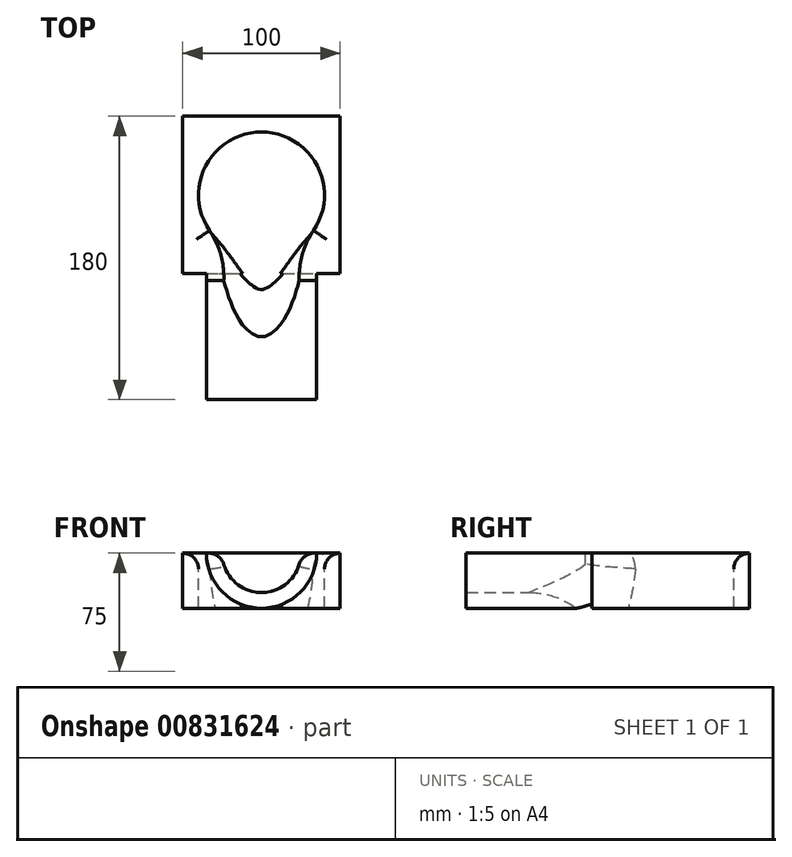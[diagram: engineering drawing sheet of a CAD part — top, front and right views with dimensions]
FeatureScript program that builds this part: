
annotation { "Feature Type Name" : "Feature", "Feature Type Description" : "" }
export const myFeature = defineFeature(function(context is Context, id is Id, definition is map)
    precondition{}
    {
        {
            var Q0;
            Q0=qCreatedBy(makeId("Front.planeOp"),FACE);
            var sketch = newSketch(context, id + "F0", { "sketchPlane" : qUnion([Q0])});
            skCircle(sketch, "E0", {"center": v(0, 0) * mm, "radius": 25 * mm});
            skCircle(sketch, "E1", {"center": v(0, 0) * mm, "radius": 35 * mm});
            skLineSegment(sketch, "E2", {"start": v(35, 0) * mm, "end": v(-35, 0) * mm});
            skSolve(sketch);
        }
        {
            var Q0;
            {var subQ0=sQuery(id+"F0.wireOp",EDGE,"E2");var subQ1=sQuery(id+"F0.wireOp",EDGE,"E0");var subQ2=makeQuery(id+"F0.imprint","INTERSECT",VERTEX,{"disambiguationData":[OD(0.0)],"derivedFrom":[subQ1,subQ0]});Q0=makeQuery(id+"F0.imprint","IMPRINT",FACE,{"disambiguationData":[TD([[makeQuery(id+"F0.imprint","IMPRINT",EDGE,{"disambiguationData":[TD([[subQ2,1.0]])],"derivedFrom":subQ1}),-1.0]])]});}
            extrude(context, id + "F1", {"entities" : qUnion([Q0]), "depth" : 80 * mm, "offsetDistance" : 25 * mm});
        }
        {
            var Q0;
            Q0=makeQuery(id+"F1.opExtrude","CAP_FACE",FACE,{"disambiguationData":[OSD([sQuery(id+"F0.wireOp",EDGE,"E0"),sQuery(id+"F0.wireOp",EDGE,"E1"),sQuery(id+"F0.wireOp",EDGE,"E2")])],"isStart":true});
            var sketch = newSketch(context, id + "F2", { "sketchPlane" : qUnion([Q0])});
            skLineSegment(sketch, "E3", {"start": v(0, -35) * mm, "end": v(0, 0) * mm, "construction": true});
            skLineSegment(sketch, "E4.bottom", {"start": v(50, 0) * mm, "end": v(-50, 0) * mm});
            skLineSegment(sketch, "E4.top", {"start": v(50, -35) * mm, "end": v(-50, -35) * mm});
            skLineSegment(sketch, "E4.left", {"start": v(50, 0) * mm, "end": v(50, -35) * mm});
            skLineSegment(sketch, "E4.right", {"start": v(-50, 0) * mm, "end": v(-50, -35) * mm});
            skPoint(sketch, "E4.middle", {"position": v(0, -17.5) * mm});
            skSolve(sketch);
        }
        {
            var Q0;
            Q0 = qSketchRegion(id + "F2", true);
            extrude(context, id + "F3", {"entities" : qUnion([Q0]), "operationType" : NewBodyOperationType.ADD, "depth" : 100 * mm, "offsetDistance" : 25 * mm});
        }
        {
            var Q0;
            {var subQ0=sQuery(id+"F0.wireOp",EDGE,"E2");var subQ1=sQuery(id+"F0.wireOp",EDGE,"E1");Q0=makeQuery(id+"F3.boolean.opBoolean","MERGE",FACE,{"derivedFrom":[makeQuery(id+"F1.opExtrude","SWEPT_FACE",FACE,{"disambiguationData":[OSD([subQ0]),TDD([makeQuery(id+"F0.imprint","IMPRINT",EDGE,{"disambiguationData":[TD([[makeQuery(id+"F0.imprint","INTERSECT",VERTEX,{"disambiguationData":[OD(0.0)],"derivedFrom":[subQ1,subQ0]}),-1.0]])],"derivedFrom":subQ0})])]}),makeQuery(id+"F1.opExtrude","SWEPT_FACE",FACE,{"disambiguationData":[OSD([subQ0]),TDD([makeQuery(id+"F0.imprint","IMPRINT",EDGE,{"disambiguationData":[TD([[makeQuery(id+"F0.imprint","INTERSECT",VERTEX,{"disambiguationData":[OD(1.0)],"derivedFrom":[subQ1,subQ0]}),1.0]])],"derivedFrom":subQ0})])]}),makeQuery(id+"F3.opExtrude","SWEPT_FACE",FACE,{"disambiguationData":[OSD([sQuery(id+"F2.wireOp",EDGE,"E4.bottom")])]})]});}
            var sketch = newSketch(context, id + "F4", { "sketchPlane" : qUnion([Q0])});
            skCircle(sketch, "E5", {"center": v(0, 50) * mm, "radius": 50 * mm});
            skPoint(sketch, "E5.first.point", {"position": v(0, 0) * mm});
            skPoint(sketch, "E5.second.point", {"position": v(-50, 50) * mm});
            skPoint(sketch, "E5.third.point", {"position": v(50, 50) * mm});
            skSolve(sketch);
        }
        {
            var Q0;
            {var subQ0=sQuery(id+"F4.wireOp",EDGE,"E5");var subQ1=sQuery(id+"F2.wireOp",EDGE,"E4.bottom");var subQ2=makeQuery(id+"F4.imprint","INTERSECT",VERTEX,{"derivedFrom":[makeQuery(id+"F3.opExtrude","CAP_EDGE",EDGE,{"disambiguationData":[OSD([subQ1])],"isStart":false}),subQ0]});Q0=makeQuery(id+"F4.imprint","IMPRINT",FACE,{"disambiguationData":[TD([[makeQuery(id+"F4.imprint","IMPRINT",EDGE,{"disambiguationData":[TD([[subQ2,1.0]])],"derivedFrom":subQ0}),1.0]])]});}
            var sketch = newSketch(context, id + "F5", { "sketchPlane" : qUnion([Q0])});
            skCircle(sketch, "E6", {"center": v(0, 50) * mm, "radius": 40 * mm});
            skSolve(sketch);
        }
        {
            var Q0;
            Q0=makeQuery(id+"F5.imprint","IMPRINT",FACE,{"disambiguationData":[TD([[makeQuery(id+"F5.imprint","IMPRINT",EDGE,{"derivedFrom":sQuery(id+"F5.wireOp",EDGE,"E6")}),1.0]])]});
            extrude(context, id + "F6", {"entities" : qUnion([Q0]), "operationType" : NewBodyOperationType.REMOVE, "endBound" : BoundingType.UP_TO_NEXT, "oppositeDirection" : true, "depth" : 25 * mm, "offsetDistance" : 25 * mm});
        }
        {
            var Q0;
            {var subQ0=sQuery(id+"F0.wireOp",EDGE,"E0");var subQ3=sQuery(id+"F2.wireOp",EDGE,"E4.bottom");Q0=makeQuery(id+"F3.boolean.opBoolean","SPLIT",FACE,{"disambiguationData":[TD([makeQuery(id+"F1.opExtrude","SWEPT_FACE",FACE,{"disambiguationData":[OSD([subQ0])]})])],"derivedFrom":makeQuery(id+"F3.opExtrude","CAP_FACE",FACE,{"disambiguationData":[OSD([subQ3,sQuery(id+"F2.wireOp",EDGE,"E4.top"),sQuery(id+"F2.wireOp",EDGE,"E4.left"),sQuery(id+"F2.wireOp",EDGE,"E4.right")])],"isStart":true})});}
            extrude(context, id + "F7", {"entities" : qUnion([Q0]), "operationType" : NewBodyOperationType.REMOVE, "oppositeDirection" : true, "depth" : 25 * mm, "offsetDistance" : 25 * mm});
        }
        {
            var Q0;
            Q0=makeQuery(id+"F7.boolean.opBoolean","INTERSECT",EDGE,{"derivedFrom":[makeQuery(id+"F6.boolean.opBoolean","COPY",FACE,{"derivedFrom":makeQuery(id+"F6.opExtrude","SWEPT_FACE",FACE,{"disambiguationData":[OSD([sQuery(id+"F5.wireOp",EDGE,"E6")])]})}),makeQuery(id+"F7.opExtrude","SWEPT_FACE",FACE,{"disambiguationData":[OSD([sQuery(id+"F0.wireOp",EDGE,"E0")])]})]});
            fillet(context, id + "F8", {"entities" : qUnion([Q0]), "radius" : 50 * mm, "tangentPropagation" : true, "allowEdgeOverflow" : false});
        }
        {
            var Q0;
            {var subQ0=sQuery(id+"F0.wireOp",EDGE,"E2");var subQ1=sQuery(id+"F0.wireOp",EDGE,"E0");var subQ2=makeQuery(id+"F0.imprint","INTERSECT",VERTEX,{"disambiguationData":[OD(0.0)],"derivedFrom":[subQ1,subQ0]});Q0=makeQuery(id+"F7.boolean.opBoolean","MERGE",EDGE,{"derivedFrom":[makeQuery(id+"F1.opExtrude","SWEPT_EDGE",EDGE,{"disambiguationData":[OSD([subQ1,subQ0]),TDD([subQ2])]}),makeQuery(id+"F7.opExtrude","SWEPT_EDGE",EDGE,{"disambiguationData":[OSD([subQ1,subQ0]),TDD([makeQuery(id+"F1.opExtrude","CAP_VERTEX",VERTEX,{"disambiguationData":[OSD([subQ1,subQ0]),TDD([subQ2])],"isStart":true})])]})]});}
            var Q1;
            Q1=makeQuery(id+"F6.boolean.opBoolean","COPY",EDGE,{"derivedFrom":makeQuery(id+"F6.opExtrude","CAP_EDGE",EDGE,{"disambiguationData":[OSD([sQuery(id+"F5.wireOp",EDGE,"E6")])],"isStart":true})});
            var Q2;
            {var subQ0=sQuery(id+"F0.wireOp",EDGE,"E2");var subQ1=sQuery(id+"F0.wireOp",EDGE,"E1");var subQ2=sQuery(id+"F0.wireOp",EDGE,"E0");Q2=makeQuery(id+"F8.opFillet","BLEND_EDGE",EDGE,{"disambiguationData":[OD(0.0)],"blendedFrom":[makeQuery(id+"F7.boolean.opBoolean","INTERSECT",EDGE,{"derivedFrom":[makeQuery(id+"F6.boolean.opBoolean","COPY",FACE,{"derivedFrom":makeQuery(id+"F6.opExtrude","SWEPT_FACE",FACE,{"disambiguationData":[OSD([sQuery(id+"F5.wireOp",EDGE,"E6")])]})}),makeQuery(id+"F7.opExtrude","SWEPT_FACE",FACE,{"disambiguationData":[OSD([subQ2])]})]}),makeQuery(id+"F3.boolean.opBoolean","MERGE",FACE,{"derivedFrom":[makeQuery(id+"F1.opExtrude","SWEPT_FACE",FACE,{"disambiguationData":[OSD([subQ0]),TDD([makeQuery(id+"F0.imprint","IMPRINT",EDGE,{"disambiguationData":[TD([[makeQuery(id+"F0.imprint","INTERSECT",VERTEX,{"disambiguationData":[OD(0.0)],"derivedFrom":[subQ1,subQ0]}),-1.0]])],"derivedFrom":subQ0})])]}),makeQuery(id+"F1.opExtrude","SWEPT_FACE",FACE,{"disambiguationData":[OSD([subQ0]),TDD([makeQuery(id+"F0.imprint","IMPRINT",EDGE,{"disambiguationData":[TD([[makeQuery(id+"F0.imprint","INTERSECT",VERTEX,{"disambiguationData":[OD(1.0)],"derivedFrom":[subQ1,subQ0]}),1.0]])],"derivedFrom":subQ0})])]}),makeQuery(id+"F3.opExtrude","SWEPT_FACE",FACE,{"disambiguationData":[OSD([sQuery(id+"F2.wireOp",EDGE,"E4.bottom")])]})]})],"blendedInto":[makeQuery(id+"F3.boolean.opBoolean","MERGE",FACE,{"derivedFrom":[makeQuery(id+"F1.opExtrude","SWEPT_FACE",FACE,{"disambiguationData":[OSD([subQ0]),TDD([makeQuery(id+"F0.imprint","IMPRINT",EDGE,{"disambiguationData":[TD([[makeQuery(id+"F0.imprint","INTERSECT",VERTEX,{"disambiguationData":[OD(0.0)],"derivedFrom":[subQ1,subQ0]}),-1.0]])],"derivedFrom":subQ0})])]}),makeQuery(id+"F1.opExtrude","SWEPT_FACE",FACE,{"disambiguationData":[OSD([subQ0]),TDD([makeQuery(id+"F0.imprint","IMPRINT",EDGE,{"disambiguationData":[TD([[makeQuery(id+"F0.imprint","INTERSECT",VERTEX,{"disambiguationData":[OD(1.0)],"derivedFrom":[subQ1,subQ0]}),1.0]])],"derivedFrom":subQ0})])]}),makeQuery(id+"F3.opExtrude","SWEPT_FACE",FACE,{"disambiguationData":[OSD([sQuery(id+"F2.wireOp",EDGE,"E4.bottom")])]})]})]});}
            var Q3;
            {var subQ0=sQuery(id+"F0.wireOp",EDGE,"E2");var subQ1=sQuery(id+"F0.wireOp",EDGE,"E1");var subQ2=sQuery(id+"F0.wireOp",EDGE,"E0");Q3=makeQuery(id+"F8.opFillet","BLEND_EDGE",EDGE,{"disambiguationData":[OD(1.0)],"blendedFrom":[makeQuery(id+"F7.boolean.opBoolean","INTERSECT",EDGE,{"derivedFrom":[makeQuery(id+"F6.boolean.opBoolean","COPY",FACE,{"derivedFrom":makeQuery(id+"F6.opExtrude","SWEPT_FACE",FACE,{"disambiguationData":[OSD([sQuery(id+"F5.wireOp",EDGE,"E6")])]})}),makeQuery(id+"F7.opExtrude","SWEPT_FACE",FACE,{"disambiguationData":[OSD([subQ2])]})]}),makeQuery(id+"F3.boolean.opBoolean","MERGE",FACE,{"derivedFrom":[makeQuery(id+"F1.opExtrude","SWEPT_FACE",FACE,{"disambiguationData":[OSD([subQ0]),TDD([makeQuery(id+"F0.imprint","IMPRINT",EDGE,{"disambiguationData":[TD([[makeQuery(id+"F0.imprint","INTERSECT",VERTEX,{"disambiguationData":[OD(0.0)],"derivedFrom":[subQ1,subQ0]}),-1.0]])],"derivedFrom":subQ0})])]}),makeQuery(id+"F1.opExtrude","SWEPT_FACE",FACE,{"disambiguationData":[OSD([subQ0]),TDD([makeQuery(id+"F0.imprint","IMPRINT",EDGE,{"disambiguationData":[TD([[makeQuery(id+"F0.imprint","INTERSECT",VERTEX,{"disambiguationData":[OD(1.0)],"derivedFrom":[subQ1,subQ0]}),1.0]])],"derivedFrom":subQ0})])]}),makeQuery(id+"F3.opExtrude","SWEPT_FACE",FACE,{"disambiguationData":[OSD([sQuery(id+"F2.wireOp",EDGE,"E4.bottom")])]})]})],"blendedInto":[makeQuery(id+"F3.boolean.opBoolean","MERGE",FACE,{"derivedFrom":[makeQuery(id+"F1.opExtrude","SWEPT_FACE",FACE,{"disambiguationData":[OSD([subQ0]),TDD([makeQuery(id+"F0.imprint","IMPRINT",EDGE,{"disambiguationData":[TD([[makeQuery(id+"F0.imprint","INTERSECT",VERTEX,{"disambiguationData":[OD(0.0)],"derivedFrom":[subQ1,subQ0]}),-1.0]])],"derivedFrom":subQ0})])]}),makeQuery(id+"F1.opExtrude","SWEPT_FACE",FACE,{"disambiguationData":[OSD([subQ0]),TDD([makeQuery(id+"F0.imprint","IMPRINT",EDGE,{"disambiguationData":[TD([[makeQuery(id+"F0.imprint","INTERSECT",VERTEX,{"disambiguationData":[OD(1.0)],"derivedFrom":[subQ1,subQ0]}),1.0]])],"derivedFrom":subQ0})])]}),makeQuery(id+"F3.opExtrude","SWEPT_FACE",FACE,{"disambiguationData":[OSD([sQuery(id+"F2.wireOp",EDGE,"E4.bottom")])]})]})]});}
            var Q4;
            {var subQ0=sQuery(id+"F0.wireOp",EDGE,"E2");var subQ1=sQuery(id+"F0.wireOp",EDGE,"E0");var subQ2=makeQuery(id+"F0.imprint","INTERSECT",VERTEX,{"disambiguationData":[OD(1.0)],"derivedFrom":[subQ1,subQ0]});Q4=makeQuery(id+"F7.boolean.opBoolean","MERGE",EDGE,{"derivedFrom":[makeQuery(id+"F1.opExtrude","SWEPT_EDGE",EDGE,{"disambiguationData":[OSD([subQ1,subQ0]),TDD([subQ2])]}),makeQuery(id+"F7.opExtrude","SWEPT_EDGE",EDGE,{"disambiguationData":[OSD([subQ1,subQ0]),TDD([makeQuery(id+"F1.opExtrude","CAP_VERTEX",VERTEX,{"disambiguationData":[OSD([subQ1,subQ0]),TDD([subQ2])],"isStart":true})])]})]});}
            fillet(context, id + "F9", {"entities" : qUnion([Q0, Q1, Q2, Q3, Q4]), "radius" : 10 * mm, "tangentPropagation" : true, "allowEdgeOverflow" : false});
        }
    });
